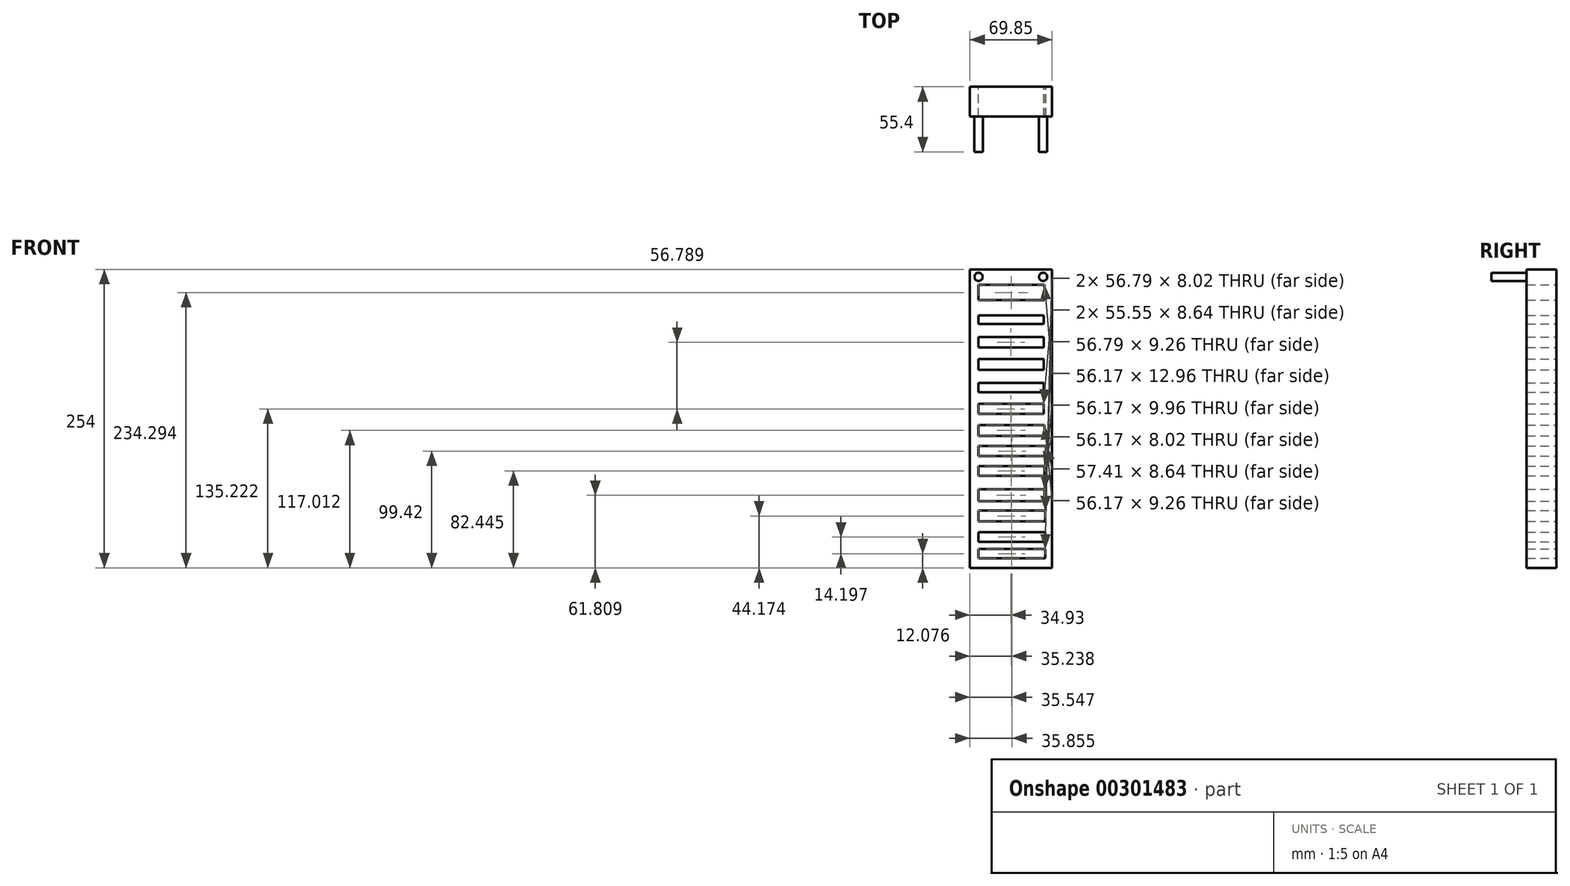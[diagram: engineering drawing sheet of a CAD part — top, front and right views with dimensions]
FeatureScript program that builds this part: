
annotation { "Feature Type Name" : "Feature", "Feature Type Description" : "" }
export const myFeature = defineFeature(function(context is Context, id is Id, definition is map)
    precondition{}
    {
        {
            var Q0;
            Q0=qCreatedBy(makeId("Front.planeOp"),FACE);
            var sketch = newSketch(context, id + "F0", { "sketchPlane" : qUnion([Q0])});
            skLineSegment(sketch, "E0.bottom", {"start": v(-35.53, 187.2) * mm, "end": v(34.32, 187.2) * mm});
            skLineSegment(sketch, "E0.top", {"start": v(-35.53, -66.8) * mm, "end": v(34.32, -66.8) * mm});
            skLineSegment(sketch, "E0.left", {"start": v(-35.53, 187.2) * mm, "end": v(-35.53, -66.8) * mm});
            skLineSegment(sketch, "E0.right", {"start": v(34.32, 187.2) * mm, "end": v(34.32, -66.8) * mm});
            skSolve(sketch);
        }
        {
            var Q0;
            Q0 = qSketchRegion(id + "F0", true);
            extrude(context, id + "F1", {"entities" : qUnion([Q0]), "depth" : 25.4 * mm});
        }
        {
            var Q0;
            Q0=makeQuery(id+"F1.opExtrude","CAP_FACE",FACE,{"disambiguationData":[OSD([sQuery(id+"F0.wireOp",EDGE,"E0.bottom"),sQuery(id+"F0.wireOp",EDGE,"E0.top"),sQuery(id+"F0.wireOp",EDGE,"E0.left"),sQuery(id+"F0.wireOp",EDGE,"E0.right")])],"isStart":true});
            var sketch = newSketch(context, id + "F2", { "sketchPlane" : qUnion([Q0])});
            skLineSegment(sketch, "E1.bottom", {"start": v(-27.8, 173.99) * mm, "end": v(28.38, 173.99) * mm});
            skLineSegment(sketch, "E1.top", {"start": v(-27.8, 161.02) * mm, "end": v(28.38, 161.02) * mm});
            skLineSegment(sketch, "E1.left", {"start": v(-27.8, 173.99) * mm, "end": v(-27.8, 161.02) * mm});
            skLineSegment(sketch, "E1.right", {"start": v(28.38, 173.99) * mm, "end": v(28.38, 161.02) * mm});
            skLineSegment(sketch, "E2.bottom", {"start": v(-27.18, 148.06) * mm, "end": v(28.38, 148.06) * mm});
            skLineSegment(sketch, "E2.top", {"start": v(-27.18, 140.65) * mm, "end": v(28.38, 140.65) * mm});
            skLineSegment(sketch, "E2.left", {"start": v(-27.18, 148.06) * mm, "end": v(-27.18, 140.65) * mm});
            skLineSegment(sketch, "E2.right", {"start": v(28.38, 148.06) * mm, "end": v(28.38, 140.65) * mm});
            skLineSegment(sketch, "E3.bottom", {"start": v(-27.18, 129.54) * mm, "end": v(28.38, 129.54) * mm});
            skLineSegment(sketch, "E3.top", {"start": v(-27.18, 120.9) * mm, "end": v(28.38, 120.9) * mm});
            skLineSegment(sketch, "E3.left", {"start": v(-27.18, 129.54) * mm, "end": v(-27.18, 120.9) * mm});
            skLineSegment(sketch, "E3.right", {"start": v(28.38, 129.54) * mm, "end": v(28.38, 120.9) * mm});
            skLineSegment(sketch, "E4.bottom", {"start": v(-27.18, 111.02) * mm, "end": v(28.38, 111.02) * mm});
            skLineSegment(sketch, "E4.top", {"start": v(-27.18, 101.76) * mm, "end": v(28.38, 101.76) * mm});
            skLineSegment(sketch, "E4.left", {"start": v(-27.18, 111.02) * mm, "end": v(-27.18, 101.76) * mm});
            skLineSegment(sketch, "E4.right", {"start": v(28.38, 111.02) * mm, "end": v(28.38, 101.76) * mm});
            skLineSegment(sketch, "E5.bottom", {"start": v(-27.18, 90.65) * mm, "end": v(28.38, 90.65) * mm});
            skLineSegment(sketch, "E5.top", {"start": v(-27.18, 82.63) * mm, "end": v(28.38, 82.63) * mm});
            skLineSegment(sketch, "E5.left", {"start": v(-27.18, 90.65) * mm, "end": v(-27.18, 82.63) * mm});
            skLineSegment(sketch, "E5.right", {"start": v(28.38, 90.65) * mm, "end": v(28.38, 82.63) * mm});
            skLineSegment(sketch, "E6.bottom", {"start": v(-27.18, 72.75) * mm, "end": v(28.38, 72.75) * mm});
            skLineSegment(sketch, "E6.top", {"start": v(-27.18, 64.11) * mm, "end": v(28.38, 64.11) * mm});
            skLineSegment(sketch, "E6.left", {"start": v(-27.18, 72.75) * mm, "end": v(-27.18, 64.11) * mm});
            skLineSegment(sketch, "E6.right", {"start": v(28.38, 72.75) * mm, "end": v(28.38, 64.11) * mm});
            skLineSegment(sketch, "E7.bottom", {"start": v(-27.8, 54.85) * mm, "end": v(28.38, 54.85) * mm});
            skLineSegment(sketch, "E7.top", {"start": v(-27.8, 45.6) * mm, "end": v(28.38, 45.6) * mm});
            skLineSegment(sketch, "E7.left", {"start": v(-27.8, 54.85) * mm, "end": v(-27.8, 45.6) * mm});
            skLineSegment(sketch, "E7.right", {"start": v(28.38, 54.85) * mm, "end": v(28.38, 45.6) * mm});
            skLineSegment(sketch, "E8.bottom", {"start": v(-29.03, 36.95) * mm, "end": v(28.38, 36.95) * mm});
            skLineSegment(sketch, "E8.top", {"start": v(-29.03, 28.3) * mm, "end": v(28.38, 28.3) * mm});
            skLineSegment(sketch, "E8.left", {"start": v(-29.03, 36.95) * mm, "end": v(-29.03, 28.3) * mm});
            skLineSegment(sketch, "E8.right", {"start": v(28.38, 36.95) * mm, "end": v(28.38, 28.3) * mm});
            skLineSegment(sketch, "E9.bottom", {"start": v(-27.8, 19.67) * mm, "end": v(28.38, 19.67) * mm});
            skLineSegment(sketch, "E9.top", {"start": v(-27.8, 11.64) * mm, "end": v(28.38, 11.64) * mm});
            skLineSegment(sketch, "E9.left", {"start": v(-27.8, 19.67) * mm, "end": v(-27.8, 11.64) * mm});
            skLineSegment(sketch, "E9.right", {"start": v(28.38, 19.67) * mm, "end": v(28.38, 11.64) * mm});
            skLineSegment(sketch, "E10.bottom", {"start": v(-27.8, 0) * mm, "end": v(28.38, 0) * mm});
            skLineSegment(sketch, "E10.top", {"start": v(-27.8, -9.96) * mm, "end": v(28.38, -9.96) * mm});
            skLineSegment(sketch, "E10.left", {"start": v(-27.8, 0) * mm, "end": v(-27.8, -9.96) * mm});
            skLineSegment(sketch, "E10.right", {"start": v(28.38, 0) * mm, "end": v(28.38, -9.96) * mm});
            skLineSegment(sketch, "E11.bottom", {"start": v(-28.41, -17.99) * mm, "end": v(28.38, -17.99) * mm});
            skLineSegment(sketch, "E11.top", {"start": v(-28.41, -27.25) * mm, "end": v(28.38, -27.25) * mm});
            skLineSegment(sketch, "E11.left", {"start": v(-28.41, -17.99) * mm, "end": v(-28.41, -27.25) * mm});
            skLineSegment(sketch, "E11.right", {"start": v(28.38, -17.99) * mm, "end": v(28.38, -27.25) * mm});
            skLineSegment(sketch, "E12.bottom", {"start": v(-28.41, -36.5) * mm, "end": v(28.38, -36.5) * mm});
            skLineSegment(sketch, "E12.top", {"start": v(-28.41, -44.53) * mm, "end": v(28.38, -44.53) * mm});
            skLineSegment(sketch, "E12.left", {"start": v(-28.41, -36.5) * mm, "end": v(-28.41, -44.53) * mm});
            skLineSegment(sketch, "E12.right", {"start": v(28.38, -36.5) * mm, "end": v(28.38, -44.53) * mm});
            skLineSegment(sketch, "E13.bottom", {"start": v(-28.41, -50.7) * mm, "end": v(28.38, -50.7) * mm});
            skLineSegment(sketch, "E13.top", {"start": v(-28.41, -58.73) * mm, "end": v(28.38, -58.73) * mm});
            skLineSegment(sketch, "E13.left", {"start": v(-28.41, -50.7) * mm, "end": v(-28.41, -58.73) * mm});
            skLineSegment(sketch, "E13.right", {"start": v(28.38, -50.7) * mm, "end": v(28.38, -58.73) * mm});
            skSolve(sketch);
        }
        {
            var Q0;
            Q0=makeQuery(id+"F2.imprint","IMPRINT",FACE,{"disambiguationData":[TD([[makeQuery(id+"F2.imprint","IMPRINT",EDGE,{"derivedFrom":sQuery(id+"F2.wireOp",EDGE,"E2.bottom")}),-1.0]])]});
            var Q1;
            Q1=makeQuery(id+"F2.imprint","IMPRINT",FACE,{"disambiguationData":[TD([[makeQuery(id+"F2.imprint","IMPRINT",EDGE,{"derivedFrom":sQuery(id+"F2.wireOp",EDGE,"E3.bottom")}),-1.0]])]});
            var Q2;
            Q2=makeQuery(id+"F2.imprint","IMPRINT",FACE,{"disambiguationData":[TD([[makeQuery(id+"F2.imprint","IMPRINT",EDGE,{"derivedFrom":sQuery(id+"F2.wireOp",EDGE,"E4.bottom")}),-1.0]])]});
            var Q3;
            Q3=makeQuery(id+"F2.imprint","IMPRINT",FACE,{"disambiguationData":[TD([[makeQuery(id+"F2.imprint","IMPRINT",EDGE,{"derivedFrom":sQuery(id+"F2.wireOp",EDGE,"E5.bottom")}),-1.0]])]});
            var Q4;
            Q4=makeQuery(id+"F2.imprint","IMPRINT",FACE,{"disambiguationData":[TD([[makeQuery(id+"F2.imprint","IMPRINT",EDGE,{"derivedFrom":sQuery(id+"F2.wireOp",EDGE,"E6.bottom")}),-1.0]])]});
            var Q5;
            Q5=makeQuery(id+"F2.imprint","IMPRINT",FACE,{"disambiguationData":[TD([[makeQuery(id+"F2.imprint","IMPRINT",EDGE,{"derivedFrom":sQuery(id+"F2.wireOp",EDGE,"E7.bottom")}),-1.0]])]});
            var Q6;
            Q6=makeQuery(id+"F2.imprint","IMPRINT",FACE,{"disambiguationData":[TD([[makeQuery(id+"F2.imprint","IMPRINT",EDGE,{"derivedFrom":sQuery(id+"F2.wireOp",EDGE,"E8.bottom")}),-1.0]])]});
            var Q7;
            Q7=makeQuery(id+"F2.imprint","IMPRINT",FACE,{"disambiguationData":[TD([[makeQuery(id+"F2.imprint","IMPRINT",EDGE,{"derivedFrom":sQuery(id+"F2.wireOp",EDGE,"E9.bottom")}),-1.0]])]});
            var Q8;
            Q8=makeQuery(id+"F2.imprint","IMPRINT",FACE,{"disambiguationData":[TD([[makeQuery(id+"F2.imprint","IMPRINT",EDGE,{"derivedFrom":sQuery(id+"F2.wireOp",EDGE,"E10.bottom")}),-1.0]])]});
            var Q9;
            Q9=makeQuery(id+"F2.imprint","IMPRINT",FACE,{"disambiguationData":[TD([[makeQuery(id+"F2.imprint","IMPRINT",EDGE,{"derivedFrom":sQuery(id+"F2.wireOp",EDGE,"E11.bottom")}),-1.0]])]});
            var Q10;
            Q10=makeQuery(id+"F2.imprint","IMPRINT",FACE,{"disambiguationData":[TD([[makeQuery(id+"F2.imprint","IMPRINT",EDGE,{"derivedFrom":sQuery(id+"F2.wireOp",EDGE,"E12.bottom")}),-1.0]])]});
            var Q11;
            Q11=makeQuery(id+"F2.imprint","IMPRINT",FACE,{"disambiguationData":[TD([[makeQuery(id+"F2.imprint","IMPRINT",EDGE,{"derivedFrom":sQuery(id+"F2.wireOp",EDGE,"E13.bottom")}),-1.0]])]});
            var Q12;
            Q12=makeQuery(id+"F2.imprint","IMPRINT",FACE,{"disambiguationData":[TD([[makeQuery(id+"F2.imprint","IMPRINT",EDGE,{"derivedFrom":sQuery(id+"F2.wireOp",EDGE,"E1.bottom")}),-1.0]])]});
            var Q13;
            Q13=makeQuery(id+"F1.opExtrude","CAP_FACE",FACE,{"disambiguationData":[OSD([sQuery(id+"F0.wireOp",EDGE,"E0.bottom"),sQuery(id+"F0.wireOp",EDGE,"E0.top"),sQuery(id+"F0.wireOp",EDGE,"E0.left"),sQuery(id+"F0.wireOp",EDGE,"E0.right")])],"isStart":false});
            extrude(context, id + "F3", {"entities" : qUnion([Q0, Q1, Q2, Q3, Q4, Q5, Q6, Q7, Q8, Q9, Q10, Q11, Q12]), "operationType" : NewBodyOperationType.REMOVE, "endBound" : BoundingType.UP_TO_SURFACE, "oppositeDirection" : true, "endBoundEntityFace" : qUnion([Q13]), "depth" : 25 * mm});
        }
        {
            var Q0;
            Q0=makeQuery(id+"F1.opExtrude","CAP_FACE",FACE,{"disambiguationData":[OSD([sQuery(id+"F0.wireOp",EDGE,"E0.bottom"),sQuery(id+"F0.wireOp",EDGE,"E0.top"),sQuery(id+"F0.wireOp",EDGE,"E0.left"),sQuery(id+"F0.wireOp",EDGE,"E0.right")])],"isStart":false});
            var sketch = newSketch(context, id + "F4", { "sketchPlane" : qUnion([Q0])});
            skCircle(sketch, "E14", {"center": v(-28.13, 180.87) * mm, "radius": 3.5 * mm});
            skCircle(sketch, "E15", {"center": v(26.78, 180.87) * mm, "radius": 3.5 * mm});
            skSolve(sketch);
        }
        {
            var Q0;
            Q0 = qSketchRegion(id + "F4", true);
            extrude(context, id + "F5", {"entities" : qUnion([Q0]), "operationType" : NewBodyOperationType.ADD, "depth" : 30 * mm});
        }
    });
